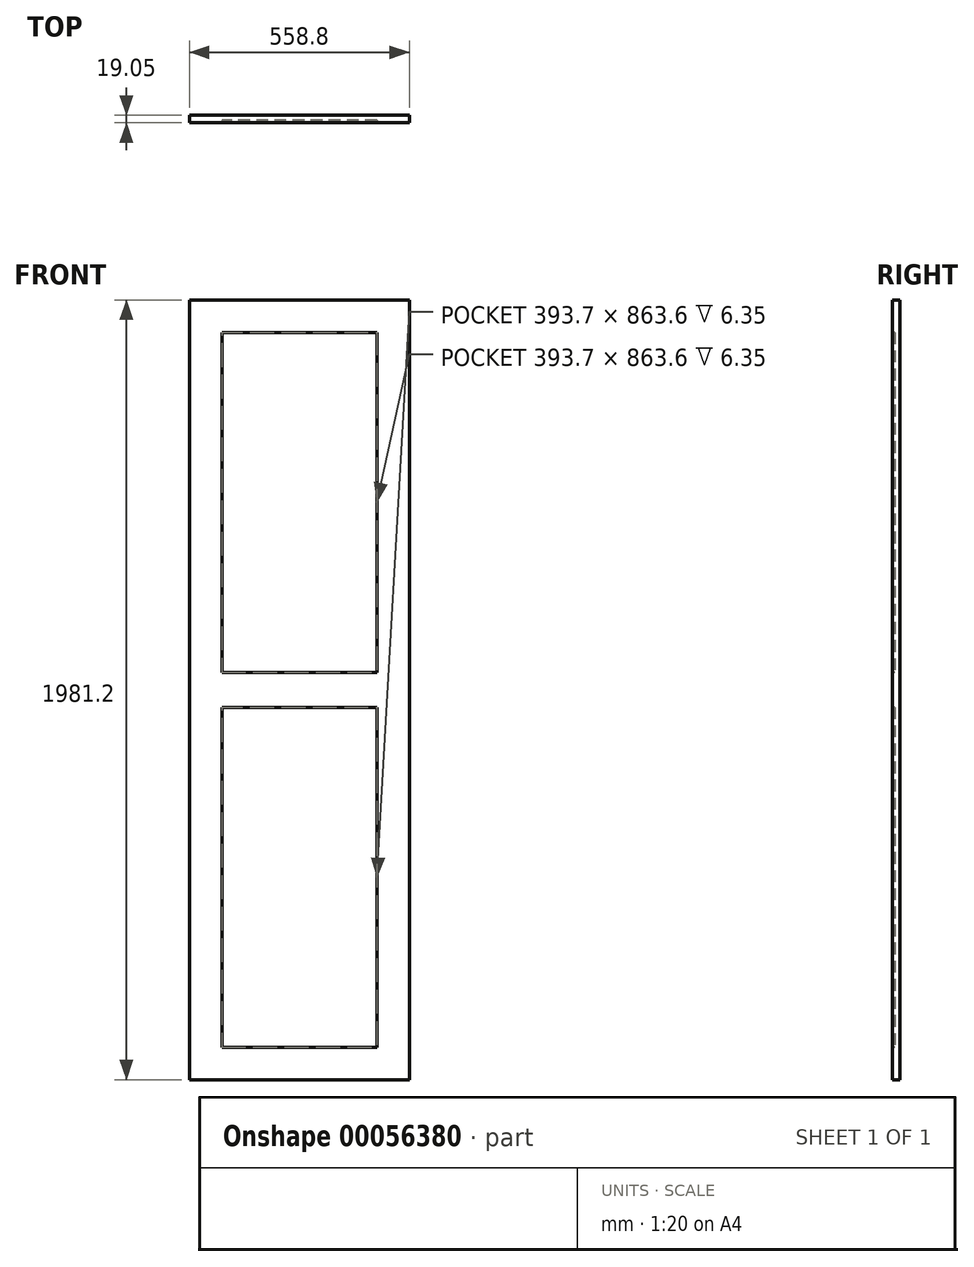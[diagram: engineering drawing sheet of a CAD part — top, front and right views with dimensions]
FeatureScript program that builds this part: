
annotation { "Feature Type Name" : "Feature", "Feature Type Description" : "" }
export const myFeature = defineFeature(function(context is Context, id is Id, definition is map)
    precondition{}
    {
        {
            var Q0;
            Q0=qCreatedBy(makeId("Front.planeOp"),FACE);
            var sketch = newSketch(context, id + "F0", { "sketchPlane" : qUnion([Q0])});
            skLineSegment(sketch, "E0.bottom", {"start": v(-278.13, 1429.77) * mm, "end": v(280.67, 1429.77) * mm});
            skLineSegment(sketch, "E0.top", {"start": v(-278.13, -551.43) * mm, "end": v(280.67, -551.43) * mm});
            skLineSegment(sketch, "E0.left", {"start": v(-278.13, 1429.77) * mm, "end": v(-278.13, -551.43) * mm});
            skLineSegment(sketch, "E0.right", {"start": v(280.67, 1429.77) * mm, "end": v(280.67, -551.43) * mm});
            skSolve(sketch);
        }
        {
            var Q0;
            Q0 = qSketchRegion(id + "F0", true);
            extrude(context, id + "F1", {"entities" : qUnion([Q0]), "oppositeDirection" : true, "depth" : 19.05 * mm});
        }
        {
            var Q0;
            Q0=makeQuery(id+"F1.opExtrude","CAP_FACE",FACE,{"disambiguationData":[OSD([sQuery(id+"F0.wireOp",EDGE,"E0.bottom"),sQuery(id+"F0.wireOp",EDGE,"E0.top"),sQuery(id+"F0.wireOp",EDGE,"E0.left"),sQuery(id+"F0.wireOp",EDGE,"E0.right")])],"isStart":true});
            var sketch = newSketch(context, id + "F2", { "sketchPlane" : qUnion([Q0])});
            skCircle(sketch, "E1", {"center": v(-278.13, 1429.77) * mm, "radius": 82.55 * mm, "construction": true});
            skLineSegment(sketch, "E2", {"start": v(-195.58, 1429.77) * mm, "end": v(-195.58, -551.43) * mm, "construction": true});
            skLineSegment(sketch, "E3", {"start": v(-278.13, 1347.22) * mm, "end": v(280.67, 1347.22) * mm, "construction": true});
            skCircle(sketch, "E4", {"center": v(280.67, 1429.77) * mm, "radius": 82.55 * mm, "construction": true});
            skLineSegment(sketch, "E5", {"start": v(198.12, 1429.77) * mm, "end": v(198.12, -551.43) * mm, "construction": true});
            skCircle(sketch, "E6", {"center": v(-278.13, -551.43) * mm, "radius": 82.55 * mm, "construction": true});
            skLineSegment(sketch, "E7", {"start": v(-278.13, -468.88) * mm, "end": v(280.67, -468.88) * mm, "construction": true});
            skLineSegment(sketch, "E8", {"start": v(-278.13, 439.17) * mm, "end": v(280.67, 439.17) * mm, "construction": true});
            skCircle(sketch, "E9", {"center": v(-278.13, 439.17) * mm, "radius": 44.45 * mm, "construction": true});
            skLineSegment(sketch, "E10", {"start": v(-278.13, 483.62) * mm, "end": v(280.67, 483.62) * mm, "construction": true});
            skLineSegment(sketch, "E11", {"start": v(-278.13, 394.72) * mm, "end": v(280.67, 394.72) * mm, "construction": true});
            skLineSegment(sketch, "E12.bottom", {"start": v(-195.58, 1347.22) * mm, "end": v(198.12, 1347.22) * mm});
            skLineSegment(sketch, "E12.top", {"start": v(-195.58, 483.62) * mm, "end": v(198.12, 483.62) * mm});
            skLineSegment(sketch, "E12.left", {"start": v(-195.58, 1347.22) * mm, "end": v(-195.58, 483.62) * mm});
            skLineSegment(sketch, "E12.right", {"start": v(198.12, 1347.22) * mm, "end": v(198.12, 483.62) * mm});
            skLineSegment(sketch, "E13.bottom", {"start": v(198.12, 394.72) * mm, "end": v(-195.58, 394.72) * mm});
            skLineSegment(sketch, "E13.top", {"start": v(198.12, -468.88) * mm, "end": v(-195.58, -468.88) * mm});
            skLineSegment(sketch, "E13.left", {"start": v(198.12, 394.72) * mm, "end": v(198.12, -468.88) * mm});
            skLineSegment(sketch, "E13.right", {"start": v(-195.58, 394.72) * mm, "end": v(-195.58, -468.88) * mm});
            skSolve(sketch);
        }
        {
            var Q0;
            Q0 = qSketchRegion(id + "F2", true);
            extrude(context, id + "F3", {"entities" : qUnion([Q0]), "operationType" : NewBodyOperationType.REMOVE, "oppositeDirection" : true, "depth" : 6.35 * mm});
        }
    });
